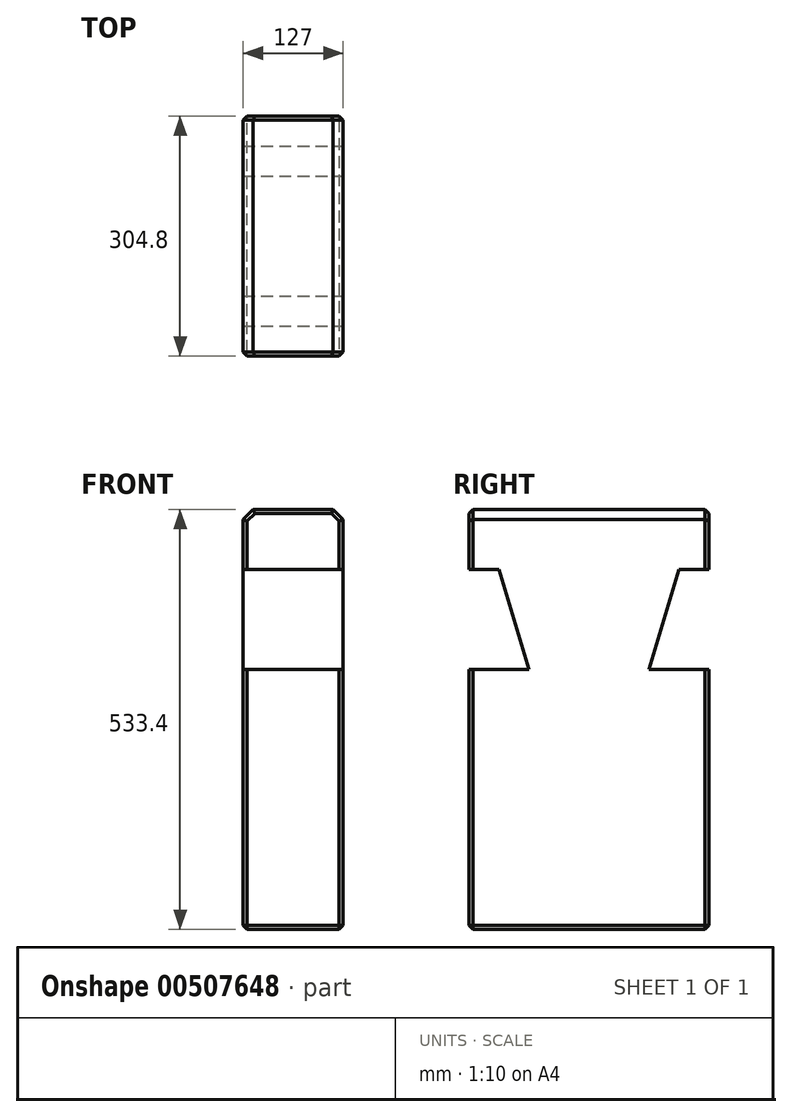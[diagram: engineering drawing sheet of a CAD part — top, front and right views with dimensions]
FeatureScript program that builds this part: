
annotation { "Feature Type Name" : "Feature", "Feature Type Description" : "" }
export const myFeature = defineFeature(function(context is Context, id is Id, definition is map)
    precondition{}
    {
        {
            var Q0;
            Q0=qCreatedBy(makeId("Right.planeOp"),FACE);
            var sketch = newSketch(context, id + "F0", { "sketchPlane" : qUnion([Q0])});
            skLineSegment(sketch, "E0.bottom", {"start": v(-152.4, 266.7) * mm, "end": v(152.4, 266.7) * mm});
            skLineSegment(sketch, "E0.top", {"start": v(-152.4, -266.7) * mm, "end": v(152.4, -266.7) * mm});
            skLineSegment(sketch, "E0.left", {"start": v(-152.4, 266.7) * mm, "end": v(-152.4, -266.7) * mm});
            skLineSegment(sketch, "E0.right", {"start": v(152.4, 266.7) * mm, "end": v(152.4, -266.7) * mm});
            skSolve(sketch);
        }
        {
            var Q0;
            Q0 = qSketchRegion(id + "F0", true);
            extrude(context, id + "F1", {"entities" : qUnion([Q0]), "depth" : 63.5 * mm, "hasSecondDirection" : true, "secondDirectionOppositeDirection" : true, "secondDirectionDepth" : 63.5 * mm});
        }
        {
            var Q0;
            Q0=makeQuery(id+"F1.opExtrude","CAP_FACE",FACE,{"disambiguationData":[OSD([sQuery(id+"F0.wireOp",EDGE,"E0.bottom"),sQuery(id+"F0.wireOp",EDGE,"E0.top"),sQuery(id+"F0.wireOp",EDGE,"E0.left"),sQuery(id+"F0.wireOp",EDGE,"E0.right")])],"isStart":false});
            var sketch = newSketch(context, id + "F2", { "sketchPlane" : qUnion([Q0])});
            skLineSegment(sketch, "E1", {"start": v(-152.4, 190.5) * mm, "end": v(-152.4, 63.5) * mm});
            skLineSegment(sketch, "E2", {"start": v(-152.4, 63.5) * mm, "end": v(-76.2, 63.5) * mm});
            skLineSegment(sketch, "E3", {"start": v(-76.2, 63.5) * mm, "end": v(-114.3, 190.5) * mm});
            skLineSegment(sketch, "E4", {"start": v(-114.3, 190.5) * mm, "end": v(-152.4, 190.5) * mm});
            skLineSegment(sketch, "E5.MirrorCS", {"start": v(114.3, 190.5) * mm, "end": v(152.4, 190.5) * mm});
            skLineSegment(sketch, "E6.MirrorCS", {"start": v(76.2, 63.5) * mm, "end": v(114.3, 190.5) * mm});
            skLineSegment(sketch, "E7.MirrorCS", {"start": v(152.4, 63.5) * mm, "end": v(76.2, 63.5) * mm});
            skLineSegment(sketch, "E8.MirrorCS", {"start": v(152.4, 190.5) * mm, "end": v(152.4, 63.5) * mm});
            skSolve(sketch);
        }
        {
            var Q0;
            Q0 = qSketchRegion(id + "F2", true);
            var Q1;
            {var subQ0=sQuery(id+"F2.wireOp",EDGE,"c423d06e-9c46-4ae4-87d4-f0093e8d50d10.MirrorCS");Q1=makeQuery(id+"F2.imprint","IMPRINT",FACE,{"disambiguationData":[TD([[makeQuery(id+"F2.imprint","IMPRINT",EDGE,{"derivedFrom":subQ0}),-1.0]])]});}
            extrude(context, id + "F3", {"entities" : qUnion([Q0, Q1]), "operationType" : NewBodyOperationType.REMOVE, "endBound" : BoundingType.UP_TO_NEXT, "oppositeDirection" : true, "depth" : 25.4 * mm});
        }
        {
            var Q0;
            Q0=makeQuery(id+"F1.opExtrude","CAP_EDGE",EDGE,{"disambiguationData":[OSD([sQuery(id+"F0.wireOp",EDGE,"E0.bottom")])],"isStart":false});
            var Q1;
            Q1=makeQuery(id+"F1.opExtrude","CAP_EDGE",EDGE,{"disambiguationData":[OSD([sQuery(id+"F0.wireOp",EDGE,"E0.bottom")])],"isStart":true});
            chamfer(context, id + "F4", {"entities" : qUnion([Q0, Q1]), "width" : 12.7 * mm, "tangentPropagation" : true});
        }
        {
            var Q0;
            Q0=makeQuery(id+"F3.boolean.opBoolean","COPY",EDGE,{"derivedFrom":makeQuery(id+"F3.opExtrude","CAP_EDGE",EDGE,{"disambiguationData":[OSD([sQuery(id+"F2.wireOp",EDGE,"E2")])],"isStart":true})});
            var Q1;
            Q1=makeQuery(id+"F3.boolean.opBoolean","COPY",EDGE,{"derivedFrom":makeQuery(id+"F3.opExtrude","CAP_EDGE",EDGE,{"disambiguationData":[OSD([sQuery(id+"F2.wireOp",EDGE,"E3")])],"isStart":true})});
            var Q2;
            Q2=makeQuery(id+"F3.boolean.opBoolean","COPY",EDGE,{"derivedFrom":makeQuery(id+"F3.opExtrude","CAP_EDGE",EDGE,{"disambiguationData":[OSD([sQuery(id+"F2.wireOp",EDGE,"E4")])],"isStart":true})});
            var Q3;
            {var subQ0=sQuery(id+"F0.wireOp",EDGE,"E0.bottom");var subQ1=sQuery(id+"F0.wireOp",EDGE,"E0.left");Q3=makeQuery(id+"F3.boolean.opBoolean","SPLIT",EDGE,{"disambiguationData":[TD([makeQuery(id+"F1.opExtrude","SWEPT_FACE",FACE,{"disambiguationData":[OSD([subQ0])]})])],"derivedFrom":makeQuery(id+"F1.opExtrude","CAP_EDGE",EDGE,{"disambiguationData":[OSD([subQ1])],"isStart":false})});}
            var Q4;
            {var subQ0=sQuery(id+"F0.wireOp",EDGE,"E0.bottom");var subQ2=sQuery(id+"F0.wireOp",EDGE,"E0.left");Q4=makeQuery(id+"F4.opChamfer","BLEND_EDGE",EDGE,{"blendedFrom":[makeQuery(id+"F1.opExtrude","CAP_EDGE",EDGE,{"disambiguationData":[OSD([subQ0])],"isStart":false}),makeQuery(id+"F3.boolean.opBoolean","SPLIT",FACE,{"disambiguationData":[TD([makeQuery(id+"F1.opExtrude","SWEPT_FACE",FACE,{"disambiguationData":[OSD([subQ0])]})])],"derivedFrom":makeQuery(id+"F1.opExtrude","SWEPT_FACE",FACE,{"disambiguationData":[OSD([subQ2])]})})],"blendedInto":[makeQuery(id+"F3.boolean.opBoolean","SPLIT",FACE,{"disambiguationData":[TD([makeQuery(id+"F1.opExtrude","SWEPT_FACE",FACE,{"disambiguationData":[OSD([subQ0])]})])],"derivedFrom":makeQuery(id+"F1.opExtrude","SWEPT_FACE",FACE,{"disambiguationData":[OSD([subQ2])]})})]});}
            var Q5;
            Q5=makeQuery(id+"F1.opExtrude","SWEPT_EDGE",EDGE,{"disambiguationData":[OSD([sQuery(id+"F0.wireOp",EDGE,"E0.bottom"),sQuery(id+"F0.wireOp",EDGE,"E0.left")])]});
            var Q6;
            {var subQ0=sQuery(id+"F0.wireOp",EDGE,"E0.bottom");var subQ1=sQuery(id+"F0.wireOp",EDGE,"E0.left");Q6=makeQuery(id+"F3.boolean.opBoolean","SPLIT",EDGE,{"disambiguationData":[TD([makeQuery(id+"F1.opExtrude","SWEPT_FACE",FACE,{"disambiguationData":[OSD([subQ0])]})])],"derivedFrom":makeQuery(id+"F1.opExtrude","CAP_EDGE",EDGE,{"disambiguationData":[OSD([subQ1])],"isStart":true})});}
            var Q7;
            Q7=makeQuery(id+"F3.boolean.opBoolean","COPY",EDGE,{"derivedFrom":makeQuery(id+"F3.opExtrude","SWEPT_EDGE",EDGE,{"disambiguationData":[OSD([sQuery(id+"F0.wireOp",EDGE,"E0.left"),sQuery(id+"F2.wireOp",EDGE,"E1"),sQuery(id+"F2.wireOp",EDGE,"E4")])]})});
            var Q8;
            Q8=makeQuery(id+"F3.boolean.opBoolean","COPY",EDGE,{"derivedFrom":makeQuery(id+"F3.opExtrude","SWEPT_EDGE",EDGE,{"disambiguationData":[OSD([sQuery(id+"F0.wireOp",EDGE,"E0.left"),sQuery(id+"F2.wireOp",EDGE,"E1"),sQuery(id+"F2.wireOp",EDGE,"E2")])]})});
            var Q9;
            Q9=makeQuery(id+"F3.boolean.opBoolean","COPY",EDGE,{"derivedFrom":makeQuery(id+"F3.opExtrude","CAP_EDGE",EDGE,{"disambiguationData":[OSD([sQuery(id+"F2.wireOp",EDGE,"E2")])],"isStart":false})});
            var Q10;
            Q10=makeQuery(id+"F3.boolean.opBoolean","COPY",EDGE,{"derivedFrom":makeQuery(id+"F3.opExtrude","CAP_EDGE",EDGE,{"disambiguationData":[OSD([sQuery(id+"F2.wireOp",EDGE,"E3")])],"isStart":false})});
            var Q11;
            Q11=makeQuery(id+"F3.boolean.opBoolean","COPY",EDGE,{"derivedFrom":makeQuery(id+"F3.opExtrude","CAP_EDGE",EDGE,{"disambiguationData":[OSD([sQuery(id+"F2.wireOp",EDGE,"E4")])],"isStart":false})});
            var Q12;
            {var subQ0=sQuery(id+"F0.wireOp",EDGE,"E0.bottom");var subQ2=sQuery(id+"F0.wireOp",EDGE,"E0.left");Q12=makeQuery(id+"F4.opChamfer","BLEND_EDGE",EDGE,{"blendedFrom":[makeQuery(id+"F1.opExtrude","CAP_EDGE",EDGE,{"disambiguationData":[OSD([subQ0])],"isStart":true}),makeQuery(id+"F3.boolean.opBoolean","SPLIT",FACE,{"disambiguationData":[TD([makeQuery(id+"F1.opExtrude","SWEPT_FACE",FACE,{"disambiguationData":[OSD([subQ0])]})])],"derivedFrom":makeQuery(id+"F1.opExtrude","SWEPT_FACE",FACE,{"disambiguationData":[OSD([subQ2])]})})],"blendedInto":[makeQuery(id+"F3.boolean.opBoolean","SPLIT",FACE,{"disambiguationData":[TD([makeQuery(id+"F1.opExtrude","SWEPT_FACE",FACE,{"disambiguationData":[OSD([subQ0])]})])],"derivedFrom":makeQuery(id+"F1.opExtrude","SWEPT_FACE",FACE,{"disambiguationData":[OSD([subQ2])]})})]});}
            var Q13;
            {var subQ0=sQuery(id+"F0.wireOp",EDGE,"E0.left");var subQ1=sQuery(id+"F0.wireOp",EDGE,"E0.top");Q13=makeQuery(id+"F3.boolean.opBoolean","SPLIT",EDGE,{"disambiguationData":[TD([makeQuery(id+"F1.opExtrude","SWEPT_FACE",FACE,{"disambiguationData":[OSD([subQ1])]})])],"derivedFrom":makeQuery(id+"F1.opExtrude","CAP_EDGE",EDGE,{"disambiguationData":[OSD([subQ0])],"isStart":true})});}
            var Q14;
            Q14=makeQuery(id+"F1.opExtrude","SWEPT_EDGE",EDGE,{"disambiguationData":[OSD([sQuery(id+"F0.wireOp",EDGE,"E0.top"),sQuery(id+"F0.wireOp",EDGE,"E0.left")])]});
            var Q15;
            {var subQ0=sQuery(id+"F0.wireOp",EDGE,"E0.left");var subQ1=sQuery(id+"F0.wireOp",EDGE,"E0.top");Q15=makeQuery(id+"F3.boolean.opBoolean","SPLIT",EDGE,{"disambiguationData":[TD([makeQuery(id+"F1.opExtrude","SWEPT_FACE",FACE,{"disambiguationData":[OSD([subQ1])]})])],"derivedFrom":makeQuery(id+"F1.opExtrude","CAP_EDGE",EDGE,{"disambiguationData":[OSD([subQ0])],"isStart":false})});}
            var Q16;
            Q16=makeQuery(id+"F1.opExtrude","CAP_EDGE",EDGE,{"disambiguationData":[OSD([sQuery(id+"F0.wireOp",EDGE,"E0.top")])],"isStart":true});
            var Q17;
            Q17=makeQuery(id+"F1.opExtrude","CAP_EDGE",EDGE,{"disambiguationData":[OSD([sQuery(id+"F0.wireOp",EDGE,"E0.top")])],"isStart":false});
            var Q18;
            Q18=makeQuery(id+"F1.opExtrude","SWEPT_EDGE",EDGE,{"disambiguationData":[OSD([sQuery(id+"F0.wireOp",EDGE,"E0.top"),sQuery(id+"F0.wireOp",EDGE,"E0.right")])]});
            var Q19;
            {var subQ0=sQuery(id+"F0.wireOp",EDGE,"E0.right");var subQ1=sQuery(id+"F0.wireOp",EDGE,"E0.top");Q19=makeQuery(id+"F3.boolean.opBoolean","SPLIT",EDGE,{"disambiguationData":[TD([makeQuery(id+"F1.opExtrude","SWEPT_FACE",FACE,{"disambiguationData":[OSD([subQ1])]})])],"derivedFrom":makeQuery(id+"F1.opExtrude","CAP_EDGE",EDGE,{"disambiguationData":[OSD([subQ0])],"isStart":false})});}
            var Q20;
            Q20=makeQuery(id+"F3.boolean.opBoolean","COPY",EDGE,{"derivedFrom":makeQuery(id+"F3.opExtrude","CAP_EDGE",EDGE,{"disambiguationData":[OSD([sQuery(id+"F2.wireOp",EDGE,"E7.MirrorCS")])],"isStart":true})});
            var Q21;
            Q21=makeQuery(id+"F3.boolean.opBoolean","COPY",EDGE,{"derivedFrom":makeQuery(id+"F3.opExtrude","CAP_EDGE",EDGE,{"disambiguationData":[OSD([sQuery(id+"F2.wireOp",EDGE,"E6.MirrorCS")])],"isStart":true})});
            var Q22;
            Q22=makeQuery(id+"F3.boolean.opBoolean","COPY",EDGE,{"derivedFrom":makeQuery(id+"F3.opExtrude","CAP_EDGE",EDGE,{"disambiguationData":[OSD([sQuery(id+"F2.wireOp",EDGE,"E5.MirrorCS")])],"isStart":true})});
            var Q23;
            {var subQ0=sQuery(id+"F0.wireOp",EDGE,"E0.bottom");var subQ1=sQuery(id+"F0.wireOp",EDGE,"E0.right");Q23=makeQuery(id+"F3.boolean.opBoolean","SPLIT",EDGE,{"disambiguationData":[TD([makeQuery(id+"F1.opExtrude","SWEPT_FACE",FACE,{"disambiguationData":[OSD([subQ0])]})])],"derivedFrom":makeQuery(id+"F1.opExtrude","CAP_EDGE",EDGE,{"disambiguationData":[OSD([subQ1])],"isStart":false})});}
            var Q24;
            {var subQ0=sQuery(id+"F0.wireOp",EDGE,"E0.bottom");var subQ1=sQuery(id+"F0.wireOp",EDGE,"E0.right");Q24=makeQuery(id+"F4.opChamfer","BLEND_EDGE",EDGE,{"blendedFrom":[makeQuery(id+"F1.opExtrude","CAP_EDGE",EDGE,{"disambiguationData":[OSD([subQ0])],"isStart":false}),makeQuery(id+"F3.boolean.opBoolean","SPLIT",FACE,{"disambiguationData":[TD([makeQuery(id+"F1.opExtrude","SWEPT_FACE",FACE,{"disambiguationData":[OSD([subQ0])]})])],"derivedFrom":makeQuery(id+"F1.opExtrude","SWEPT_FACE",FACE,{"disambiguationData":[OSD([subQ1])]})})],"blendedInto":[makeQuery(id+"F3.boolean.opBoolean","SPLIT",FACE,{"disambiguationData":[TD([makeQuery(id+"F1.opExtrude","SWEPT_FACE",FACE,{"disambiguationData":[OSD([subQ0])]})])],"derivedFrom":makeQuery(id+"F1.opExtrude","SWEPT_FACE",FACE,{"disambiguationData":[OSD([subQ1])]})})]});}
            var Q25;
            Q25=makeQuery(id+"F1.opExtrude","SWEPT_EDGE",EDGE,{"disambiguationData":[OSD([sQuery(id+"F0.wireOp",EDGE,"E0.bottom"),sQuery(id+"F0.wireOp",EDGE,"E0.right")])]});
            var Q26;
            {var subQ0=sQuery(id+"F0.wireOp",EDGE,"E0.bottom");var subQ1=sQuery(id+"F0.wireOp",EDGE,"E0.right");Q26=makeQuery(id+"F4.opChamfer","BLEND_EDGE",EDGE,{"blendedFrom":[makeQuery(id+"F1.opExtrude","CAP_EDGE",EDGE,{"disambiguationData":[OSD([subQ0])],"isStart":true}),makeQuery(id+"F3.boolean.opBoolean","SPLIT",FACE,{"disambiguationData":[TD([makeQuery(id+"F1.opExtrude","SWEPT_FACE",FACE,{"disambiguationData":[OSD([subQ0])]})])],"derivedFrom":makeQuery(id+"F1.opExtrude","SWEPT_FACE",FACE,{"disambiguationData":[OSD([subQ1])]})})],"blendedInto":[makeQuery(id+"F3.boolean.opBoolean","SPLIT",FACE,{"disambiguationData":[TD([makeQuery(id+"F1.opExtrude","SWEPT_FACE",FACE,{"disambiguationData":[OSD([subQ0])]})])],"derivedFrom":makeQuery(id+"F1.opExtrude","SWEPT_FACE",FACE,{"disambiguationData":[OSD([subQ1])]})})]});}
            var Q27;
            {var subQ0=sQuery(id+"F0.wireOp",EDGE,"E0.bottom");var subQ1=sQuery(id+"F0.wireOp",EDGE,"E0.right");Q27=makeQuery(id+"F3.boolean.opBoolean","SPLIT",EDGE,{"disambiguationData":[TD([makeQuery(id+"F1.opExtrude","SWEPT_FACE",FACE,{"disambiguationData":[OSD([subQ0])]})])],"derivedFrom":makeQuery(id+"F1.opExtrude","CAP_EDGE",EDGE,{"disambiguationData":[OSD([subQ1])],"isStart":true})});}
            var Q28;
            Q28=makeQuery(id+"F3.boolean.opBoolean","COPY",EDGE,{"derivedFrom":makeQuery(id+"F3.opExtrude","CAP_EDGE",EDGE,{"disambiguationData":[OSD([sQuery(id+"F2.wireOp",EDGE,"E5.MirrorCS")])],"isStart":false})});
            var Q29;
            Q29=makeQuery(id+"F3.boolean.opBoolean","COPY",EDGE,{"derivedFrom":makeQuery(id+"F3.opExtrude","CAP_EDGE",EDGE,{"disambiguationData":[OSD([sQuery(id+"F2.wireOp",EDGE,"E6.MirrorCS")])],"isStart":false})});
            var Q30;
            Q30=makeQuery(id+"F3.boolean.opBoolean","COPY",EDGE,{"derivedFrom":makeQuery(id+"F3.opExtrude","SWEPT_EDGE",EDGE,{"disambiguationData":[OSD([sQuery(id+"F0.wireOp",EDGE,"E0.right"),sQuery(id+"F2.wireOp",EDGE,"E5.MirrorCS"),sQuery(id+"F2.wireOp",EDGE,"E8.MirrorCS")])]})});
            var Q31;
            Q31=makeQuery(id+"F3.boolean.opBoolean","COPY",EDGE,{"derivedFrom":makeQuery(id+"F3.opExtrude","CAP_EDGE",EDGE,{"disambiguationData":[OSD([sQuery(id+"F2.wireOp",EDGE,"E7.MirrorCS")])],"isStart":false})});
            var Q32;
            Q32=makeQuery(id+"F3.boolean.opBoolean","COPY",EDGE,{"derivedFrom":makeQuery(id+"F3.opExtrude","SWEPT_EDGE",EDGE,{"disambiguationData":[OSD([sQuery(id+"F0.wireOp",EDGE,"E0.right"),sQuery(id+"F2.wireOp",EDGE,"E7.MirrorCS"),sQuery(id+"F2.wireOp",EDGE,"E8.MirrorCS")])]})});
            var Q33;
            {var subQ0=sQuery(id+"F0.wireOp",EDGE,"E0.right");var subQ1=sQuery(id+"F0.wireOp",EDGE,"E0.top");Q33=makeQuery(id+"F3.boolean.opBoolean","SPLIT",EDGE,{"disambiguationData":[TD([makeQuery(id+"F1.opExtrude","SWEPT_FACE",FACE,{"disambiguationData":[OSD([subQ1])]})])],"derivedFrom":makeQuery(id+"F1.opExtrude","CAP_EDGE",EDGE,{"disambiguationData":[OSD([subQ0])],"isStart":true})});}
            chamfer(context, id + "F5", {"entities" : qUnion([Q0, Q1, Q2, Q3, Q4, Q5, Q6, Q7, Q8, Q9, Q10, Q11, Q12, Q13, Q14, Q15, Q16, Q17, Q18, Q19, Q20, Q21, Q22, Q23, Q24, Q25, Q26, Q27, Q28, Q29, Q30, Q31, Q32, Q33]), "width" : 5.08 * mm, "tangentPropagation" : true});
        }
    });
